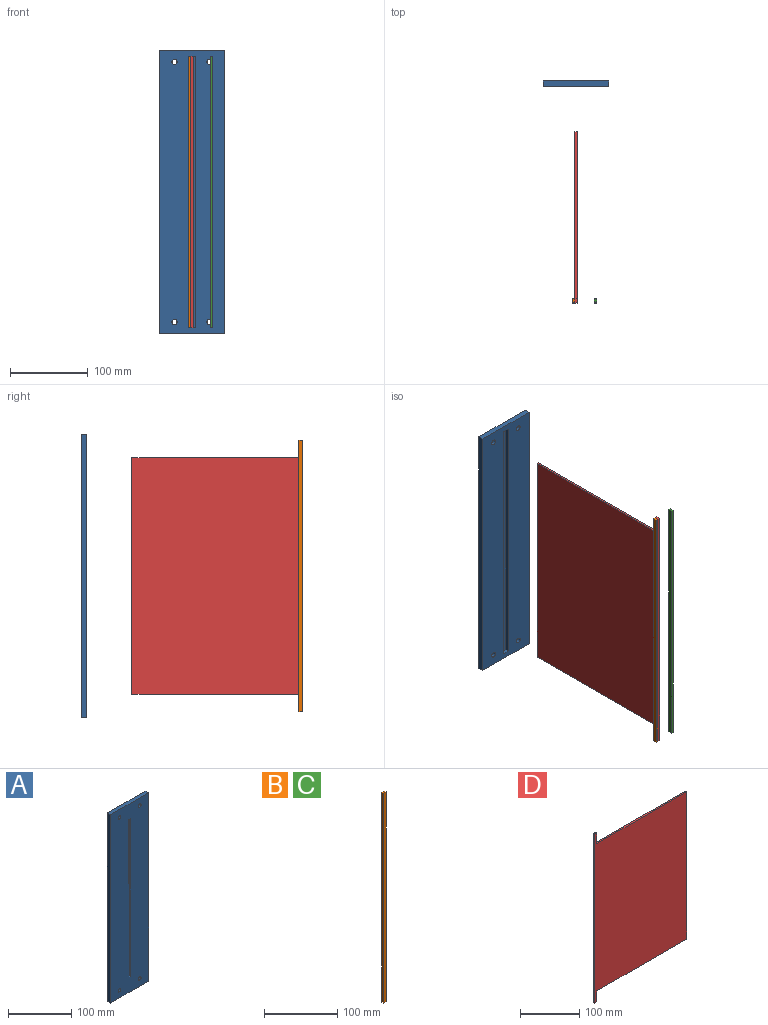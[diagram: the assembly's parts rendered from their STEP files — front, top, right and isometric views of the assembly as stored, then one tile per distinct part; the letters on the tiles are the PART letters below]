
ASSEMBLY  parts=4 mates=3
PART A: 19 faces, bbox 85x7x365 mm
  f0: plane 365x85mm, normal (0,1,0), area 27738.2mm2, adj f1,f2,f3,f4,f6,f7,f8,f9
  f1: plane 365x7mm, normal (-1,0,0), area 2555mm2, adj f0,f2,f4,f5
  f2: plane 85x7mm, normal (0,0,-1), area 595mm2, adj f0,f1,f3,f5
  f3: plane 365x7mm, normal (1,0,0), area 2555mm2, adj f0,f2,f4,f5
  f4: plane 85x7mm, normal (0,0,1), area 595mm2, adj f0,f1,f3,f5
  f5: plane 365x85mm, normal (0,-1,0), area 29973.2mm2, adj f1,f2,f3,f4,f6,f7,f8,f9
  f6: cylinder r=3.3mm len=7mm, axis (0,1,0), area 145.1mm2, adj f0,f5
  f7: cylinder r=3.3mm len=7mm, axis (0,1,0), area 145.1mm2, adj f0,f5
  f8: cylinder r=3.3mm len=7mm, axis (0,1,0), area 145.1mm2, adj f0,f5
  f9: cylinder r=3.3mm len=7mm, axis (0,1,0), area 145.1mm2, adj f0,f5
  f10: plane 350x5mm, normal (1,0,0), area 1750mm2, adj f0,f11,f13,f14
  f11: plane 9x5mm, normal (0,0,1), area 45mm2, adj f0,f10,f12,f14
  f12: plane 350x5mm, normal (-1,0,0), area 1750mm2, adj f0,f11,f13,f14
  f13: plane 9x5mm, normal (0,0,-1), area 45mm2, adj f0,f10,f12,f14
  f14: plane 350x9mm, normal (0,1,0), area 2235mm2, adj f10,f11,f12,f13,f15,f16,f17,f18
  f15: plane 305x2mm, normal (1,0,0), area 610mm2, adj f5,f14,f16,f18
  f16: plane 3x2mm, normal (0,0,1), area 6mm2, adj f5,f14,f15,f17
  f17: plane 305x2mm, normal (-1,0,0), area 610mm2, adj f5,f14,f16,f18
  f18: plane 3x2mm, normal (0,0,-1), area 6mm2, adj f5,f14,f15,f17
PART B: 6 faces, bbox 5x3x350 mm
  f0: plane 5x3mm, normal (0,0,1), area 15mm2, adj f1,f3,f4,f5
  f1: plane 350x3mm, normal (-1,0,0), area 1050mm2, adj f0,f2,f4,f5
  f2: plane 5x3mm, normal (0,0,-1), area 15mm2, adj f1,f3,f4,f5
  f3: plane 350x3mm, normal (1,0,0), area 1050mm2, adj f0,f2,f4,f5
  f4: plane 350x5mm, normal (0,-1,0), area 1750mm2, adj f0,f1,f2,f3
  f5: plane 350x5mm, normal (0,1,0), area 1750mm2, adj f0,f1,f2,f3
PART C: same geometry as B
PART D: 10 faces, bbox 220x3x350 mm
  f0: plane 215x3mm, normal (0,0,1), area 645mm2, adj f1,f7,f8,f9
  f1: plane 22.5x3mm, normal (1,0,0), area 67.5mm2, adj f0,f2,f8,f9
  f2: plane 5x3mm, normal (0,0,1), area 15mm2, adj f1,f3,f8,f9
  f3: plane 350x3mm, normal (-1,0,0), area 1050mm2, adj f2,f4,f8,f9
  f4: plane 5x3mm, normal (0,0,-1), area 15mm2, adj f3,f5,f8,f9
  f5: plane 22.5x3mm, normal (1,0,0), area 67.5mm2, adj f4,f6,f8,f9
  f6: plane 215x3mm, normal (0,0,-1), area 645mm2, adj f5,f7,f8,f9
  f7: plane 305x3mm, normal (1,0,0), area 915mm2, adj f0,f6,f8,f9
  f8: plane 350x220mm, normal (0,-1,0), area 67325mm2, adj f0,f1,f2,f3,f4,f5,f6,f7
  f9: plane 350x220mm, normal (0,1,0), area 67325mm2, adj f0,f1,f2,f3,f4,f5,f6,f7
PLACE A rot(axis=(0,0,1),180deg) t=(22.98,283.3,238.95)mm
PLACE B rot(axis=(0,0,-1),90deg) t=(21.48,-29.05,214.12)mm
PLACE C rot(axis=(0,0,-1),90deg) t=(49.4,-29.05,214.12)mm
PLACE D rot(axis=(-0.71,-0.71,0),180deg) t=(24.48,4.94,238.95)mm fixed
MATE slider C.f4 <-> D.f9  axis (-1,0,0) through (46.4,7.44,413.95)mm
MATE slider A.f14 <-> D.f5  axis (0,-1,0) through (22.98,288.3,413.95)mm
MATE slider B.f5 <-> D.f8  axis (1,0,0) through (21.48,7.44,413.95)mm
